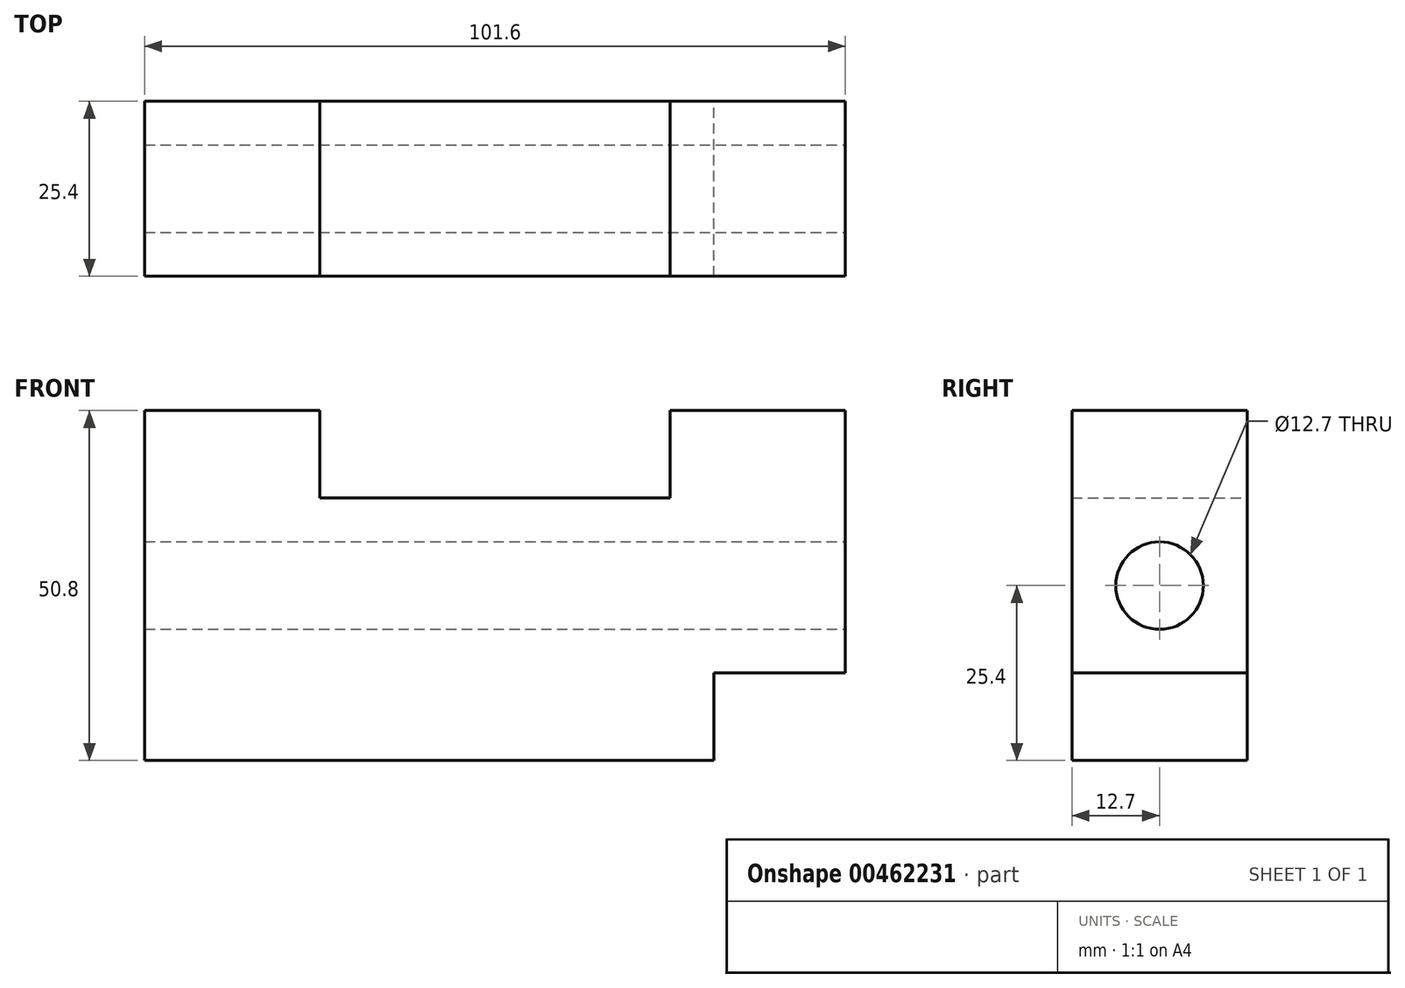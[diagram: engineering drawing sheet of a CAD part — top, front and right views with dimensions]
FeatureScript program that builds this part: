
annotation { "Feature Type Name" : "Feature", "Feature Type Description" : "" }
export const myFeature = defineFeature(function(context is Context, id is Id, definition is map)
    precondition{}
    {
        {
            var Q0;
            Q0=qCreatedBy(makeId("Front.planeOp"),FACE);
            var sketch = newSketch(context, id + "F0", { "sketchPlane" : qUnion([Q0])});
            skLineSegment(sketch, "E0.bottom", {"start": v(-50.8, 25.4) * mm, "end": v(50.8, 25.4) * mm});
            skLineSegment(sketch, "E0.top", {"start": v(-50.8, -25.4) * mm, "end": v(50.8, -25.4) * mm});
            skLineSegment(sketch, "E0.left", {"start": v(-50.8, 25.4) * mm, "end": v(-50.8, -25.4) * mm});
            skLineSegment(sketch, "E0.right", {"start": v(50.8, 25.4) * mm, "end": v(50.8, -25.4) * mm});
            skPoint(sketch, "E0.middle", {"position": v(0, 0) * mm});
            skSolve(sketch);
        }
        {
            var Q0;
            Q0=qCreatedBy(makeId("Front.planeOp"),FACE);
            var sketch = newSketch(context, id + "F1", { "sketchPlane" : qUnion([Q0])});
            skLineSegment(sketch, "E1.bottom", {"start": v(-25.4, 25.4) * mm, "end": v(25.4, 25.4) * mm});
            skLineSegment(sketch, "E1.top", {"start": v(-25.4, 12.7) * mm, "end": v(25.4, 12.7) * mm});
            skLineSegment(sketch, "E1.left", {"start": v(-25.4, 25.4) * mm, "end": v(-25.4, 12.7) * mm});
            skLineSegment(sketch, "E1.right", {"start": v(25.4, 25.4) * mm, "end": v(25.4, 12.7) * mm});
            skSolve(sketch);
        }
        {
            var Q0;
            Q0 = qSketchRegion(id + "F0", true);
            extrude(context, id + "F2", {"entities" : qUnion([Q0]), "depth" : 25.4 * mm});
        }
        {
            var Q0;
            Q0 = qSketchRegion(id + "F1", true);
            var Q1;
            Q1 = qSketchRegion(id + "F4", true);
            extrude(context, id + "F3", {"entities" : qUnion([Q0, Q1]), "operationType" : NewBodyOperationType.REMOVE, "endBound" : BoundingType.THROUGH_ALL, "depth" : 25.4 * mm});
        }
        {
            var Q0;
            Q0=qCreatedBy(makeId("Front.planeOp"),FACE);
            var sketch = newSketch(context, id + "F4", { "sketchPlane" : qUnion([Q0])});
            skLineSegment(sketch, "E2.bottom", {"start": v(50.8, -25.4) * mm, "end": v(31.75, -25.4) * mm});
            skLineSegment(sketch, "E2.top", {"start": v(50.8, -12.7) * mm, "end": v(31.75, -12.7) * mm});
            skLineSegment(sketch, "E2.left", {"start": v(50.8, -25.4) * mm, "end": v(50.8, -12.7) * mm});
            skLineSegment(sketch, "E2.right", {"start": v(31.75, -25.4) * mm, "end": v(31.75, -12.7) * mm});
            skSolve(sketch);
        }
        {
            var Q0;
            Q0 = qSketchRegion(id + "F4", true);
            extrude(context, id + "F5", {"entities" : qUnion([Q0]), "operationType" : NewBodyOperationType.REMOVE, "depth" : 25.4 * mm});
        }
        {
            var Q0;
            Q0=qCreatedBy(makeId("Right.planeOp"),FACE);
            var sketch = newSketch(context, id + "F6", { "sketchPlane" : qUnion([Q0])});
            skCircle(sketch, "E3", {"center": v(-12.7, 0) * mm, "radius": 6.35 * mm});
            skPoint(sketch, "E3.first.point", {"position": v(-14.22, 6.17) * mm});
            skPoint(sketch, "E3.second.point", {"position": v(-6.8, -2.37) * mm});
            skPoint(sketch, "E3.third.point", {"position": v(-12.84, -6.35) * mm});
            skSolve(sketch);
        }
        {
            var Q0;
            Q0 = qSketchRegion(id + "F6", true);
            extrude(context, id + "F7", {"entities" : qUnion([Q0]), "operationType" : NewBodyOperationType.REMOVE, "endBound" : BoundingType.THROUGH_ALL, "oppositeDirection" : true, "depth" : 25.4 * mm});
        }
        {
            var Q0;
            Q0 = qSketchRegion(id + "F6", true);
            extrude(context, id + "F8", {"entities" : qUnion([Q0]), "operationType" : NewBodyOperationType.REMOVE, "depth" : 50.8 * mm});
        }
    });
